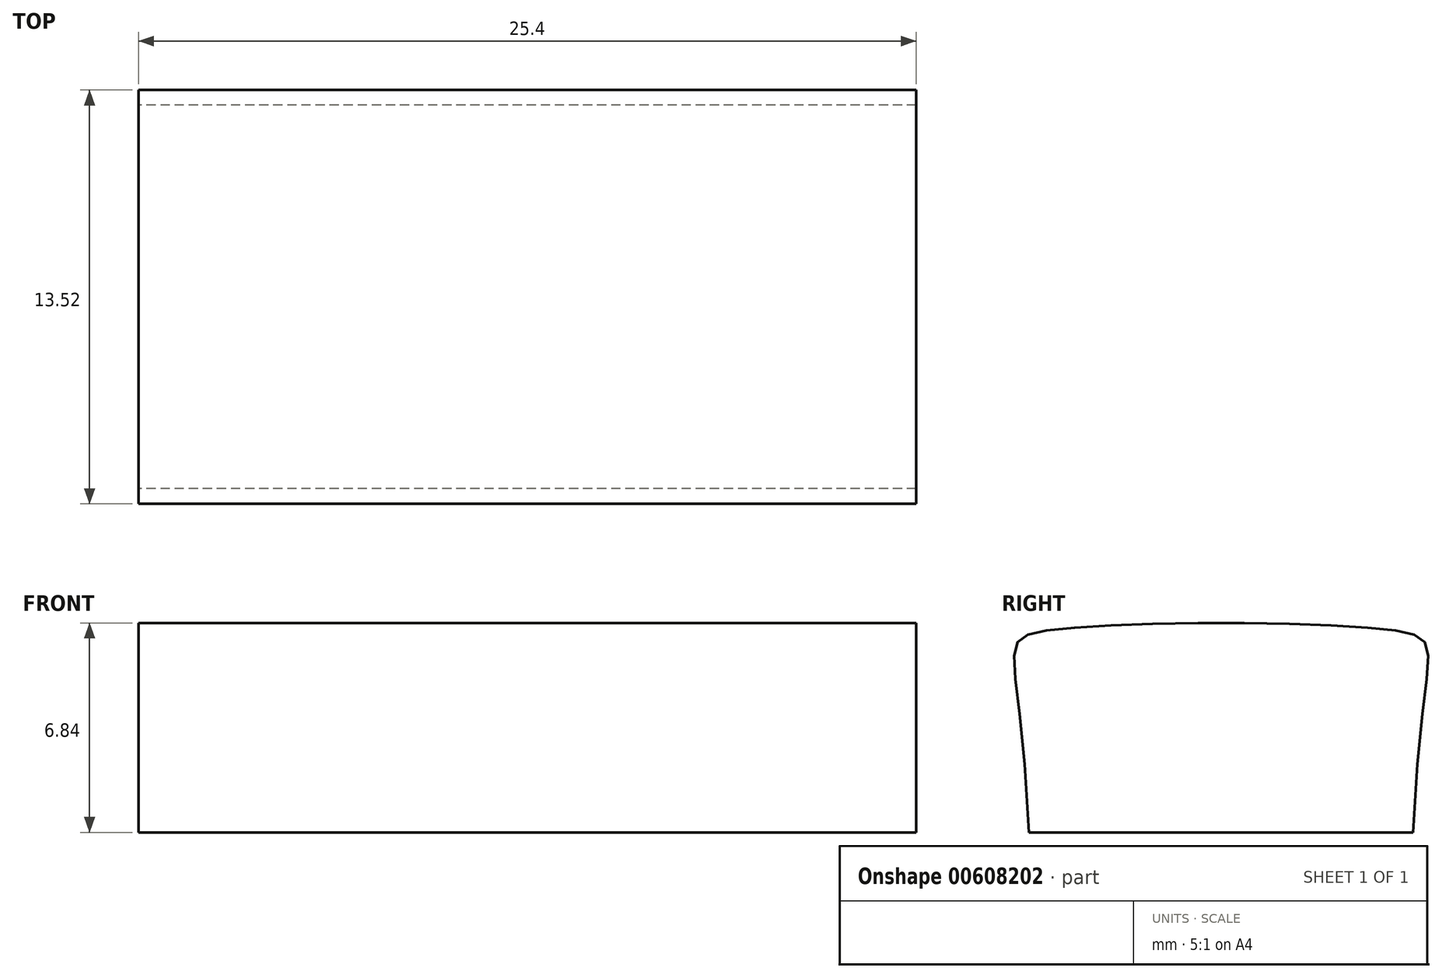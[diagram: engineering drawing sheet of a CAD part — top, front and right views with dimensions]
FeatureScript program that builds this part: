
annotation { "Feature Type Name" : "Feature", "Feature Type Description" : "" }
export const myFeature = defineFeature(function(context is Context, id is Id, definition is map)
    precondition{}
    {
        {
            var Q0;
            Q0=qCreatedBy(makeId("Right.planeOp"),FACE);
            var sketch = newSketch(context, id + "F0", { "sketchPlane" : qUnion([Q0])});
            skFitSpline(sketch, "E0", {"points": [v(-6.27, 0) * mm, v(-5.76, 6.59) * mm, v(5.76, 6.59) * mm, v(6.27, 0) * mm], "startDerivative": vector(-2.45, 58.7) * mm, "endDerivative": vector(-2.45, -58.7) * mm});
            skLineSegment(sketch, "E1", {"start": v(-6.27, 0) * mm, "end": v(6.27, 0) * mm});
            skSolve(sketch);
        }
        {
            var Q0;
            Q0 = qSketchRegion(id + "F0", true);
            extrude(context, id + "F1", {"entities" : qUnion([Q0]), "depth" : 25.4 * mm, "offsetDistance" : 25.4 * mm});
        }
    });
